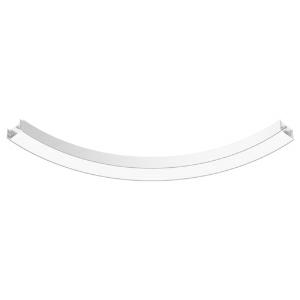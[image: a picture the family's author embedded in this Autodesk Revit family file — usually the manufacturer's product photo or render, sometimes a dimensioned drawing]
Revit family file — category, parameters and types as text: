
# Revit family: super-g_super-g__3100___90deg_hl__dir_indirekt_led__55_2w_8520lm_3000k_cri_80_430-1480_de30
name_source: partatom
category: Leuchten
revit_build: Autodesk Revit 2016 (Build: 20190508_0715(x64)
units: mm (PartAtom-declared; Revit-internal decimal feet)

## family parameters
Basisbauteil = Fläche
Beim Laden mit Abzugskörper schneiden = Nein
Bemaßung runder Anschluss = Durchmesser verwenden
Gemeinsam genutzt = Nein
Lichtquelle = Nein
Raumberechnungspunkt = Nein
Teiletyp = Normal

## types (1)
- 430-1480- (1 x LED, 1065 lm, 3000K)
    Approval mark = CE
    Beschreibung = The insert consists of aluminum-extruded profile. Charming SOFT-EDGE design ensure unparalleled styling. The ballast is integrated and allows for an operation with 220-240V (50/60Hz). SUPER-G (# 430-1480) ist not dimmable (on/off).
    CIE Flux Codes = 48 80 96 61 70
    Color Rendering = 1B/80…89
    Color Temperature = 3000K
    Height = 120 mm
    Hersteller = Prolicht
    Lamp Light Flux = 1065 lm
    Lamp count = 1
    Lampe = 1 x LED
    Length = 304 mm  [stored 0.997375 ft]
    Luminous efficacy = 98 lm/W
    ModVariant = Nein
    Modell = 430-1480
    Mounting Place = Ceiling
    Mounting Type = Pendant
    Number of Poles = 1
    OnlyDefault = Ja
    Power Factor = 1
    Product Name = SUPER-G__SUPER-G  3100 / 90° HL  dir/indirekt LED: 55,2W 8520lm 3000K CRI:80
    Product group = Suspended profile systems
    ProductGroupID = 944
    Protection Class = Protection class I
    Protection Degree = IP 20
    RLX_Detail_Level = 1
    RlxData = <blob elided: 32241 chars, md5=351f179e>
    Scheinlast = 61 VA
    Socket = socket
    Standby Power = 0 W
    System Light Flux = 5948 lm
    System Power = 61 W
    Typenbild = 430-1480.jpg
    URL = http://relux.com
    VarID = 430-1480-
    Voltage = 0 V
    Vorgabe-Ansicht = 1800 mm
    Weight = 0.00 kg
    Width = 150 mm

note: [stored X ft] marks values corroborated as IEEE doubles in the binary element streams (Revit-internal decimal feet)

## geometry (parser evidence)
native form markers: Blend x4, Sweep x41
no freeform markers — native parametric forms only
